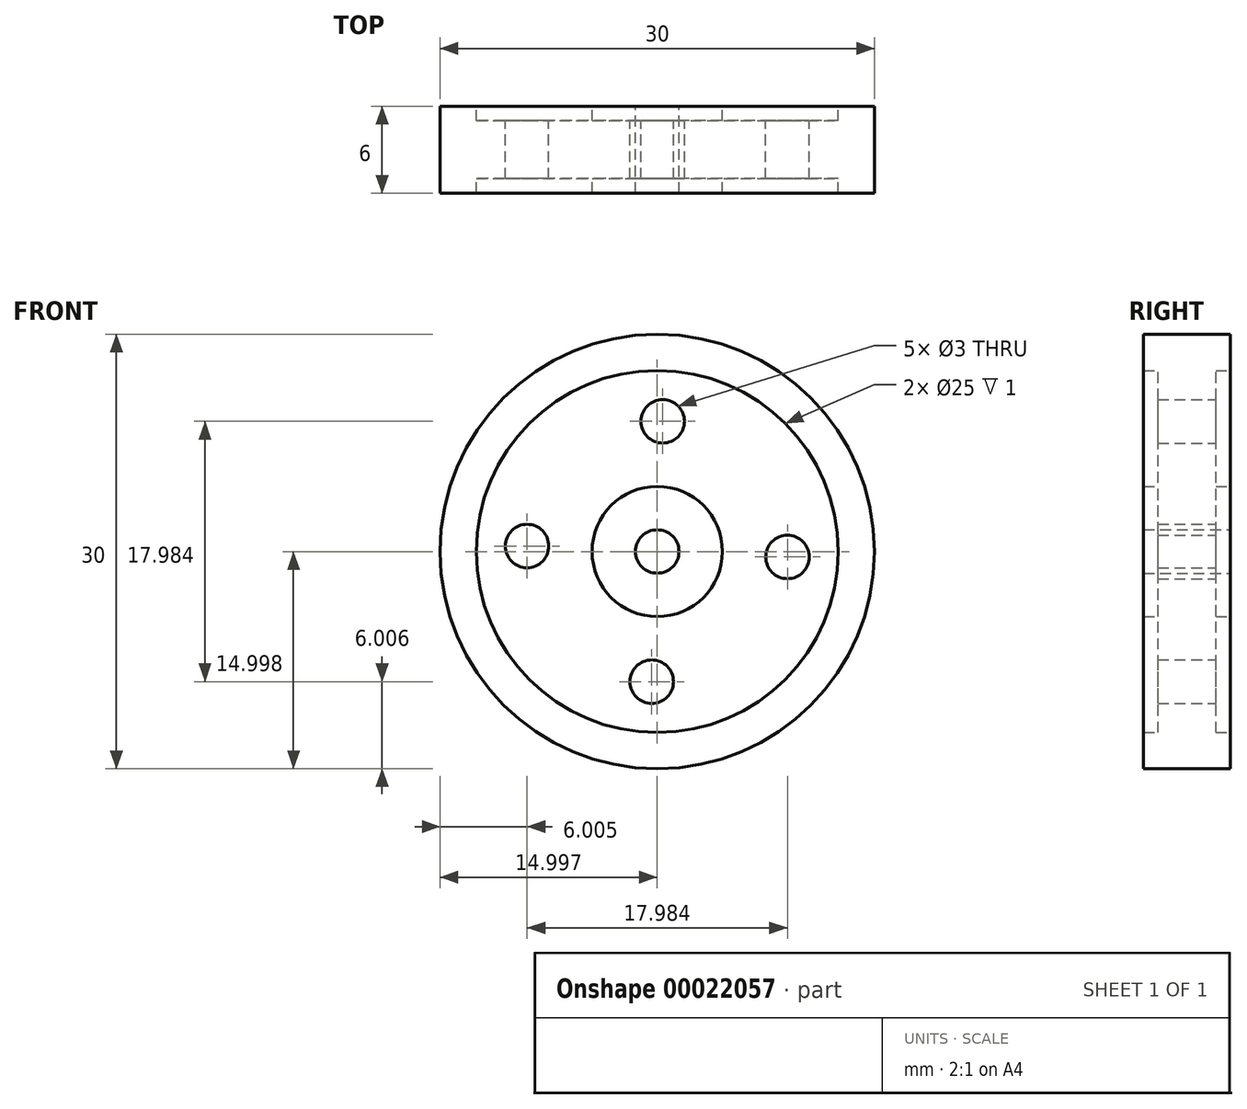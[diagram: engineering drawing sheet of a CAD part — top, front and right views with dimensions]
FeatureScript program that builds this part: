
annotation { "Feature Type Name" : "Feature", "Feature Type Description" : "" }
export const myFeature = defineFeature(function(context is Context, id is Id, definition is map)
    precondition{}
    {
        {
            var Q0;
            Q0=qCreatedBy(makeId("Front.planeOp"),FACE);
            var sketch = newSketch(context, id + "F0", { "sketchPlane" : qUnion([Q0])});
            skCircle(sketch, "E0.1.0", {"center": v(-57.19, 17.07) * mm, "radius": 1.5 * mm});
            skCircle(sketch, "E0.2.0", {"center": v(-48.57, 7.7) * mm, "radius": 1.5 * mm});
            skCircle(sketch, "E1", {"center": v(-48.2, 16.69) * mm, "radius": 15 * mm});
            skCircle(sketch, "E0.3.0", {"center": v(-39.2, 16.3) * mm, "radius": 1.5 * mm});
            skCircle(sketch, "E2", {"center": v(-48.2, 16.69) * mm, "radius": 4.5 * mm});
            skCircle(sketch, "E3", {"center": v(-47.81, 25.68) * mm, "radius": 1.5 * mm});
            skCircle(sketch, "E4", {"center": v(-48.2, 16.69) * mm, "radius": 1.5 * mm});
            skCircle(sketch, "E5", {"center": v(-48.2, 16.69) * mm, "radius": 12.5 * mm});
            skSolve(sketch);
        }
        {
            var Q0;
            Q0=makeQuery(id+"F0.imprint","IMPRINT",FACE,{"disambiguationData":[TD([[makeQuery(id+"F0.imprint","IMPRINT",EDGE,{"derivedFrom":sQuery(id+"F0.wireOp",EDGE,"E1")}),1.0]])]});
            extrude(context, id + "F1", {"entities" : qUnion([Q0]), "endBound" : BoundingType.SYMMETRIC, "depth" : 6 * mm});
        }
        {
            var Q0;
            Q0=makeQuery(id+"F0.imprint","IMPRINT",FACE,{"disambiguationData":[TD([[makeQuery(id+"F0.imprint","IMPRINT",EDGE,{"derivedFrom":sQuery(id+"F0.wireOp",EDGE,"E0.1.0")}),-1.0]])]});
            extrude(context, id + "F2", {"entities" : qUnion([Q0]), "operationType" : NewBodyOperationType.ADD, "endBound" : BoundingType.SYMMETRIC, "depth" : 4 * mm});
        }
        {
            var Q0;
            Q0=makeQuery(id+"F0.imprint","IMPRINT",FACE,{"disambiguationData":[TD([[makeQuery(id+"F0.imprint","IMPRINT",EDGE,{"derivedFrom":sQuery(id+"F0.wireOp",EDGE,"E2")}),1.0]])]});
            extrude(context, id + "F3", {"entities" : qUnion([Q0]), "operationType" : NewBodyOperationType.ADD, "endBound" : BoundingType.SYMMETRIC, "depth" : 6 * mm});
        }
    });
